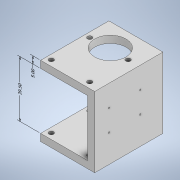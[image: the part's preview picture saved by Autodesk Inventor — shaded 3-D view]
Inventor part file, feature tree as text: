
AUTODESK INVENTOR PART (.ipt)
format: ipt  version: 2022 (Build 260153000, 153)  size: 168,448 bytes
history: native  units: mm
features: sketch x5, other x3, hole x3, extrude x2
ambient origin geometry x8: Origin, YZ Plane, XZ Plane, XY Plane, X Axis, Y Axis, Z Axis, Center Point
bodies: Body1 (feature_tree)
feature tree (13):
  other  "ソリッド1"
  extrude  "押し出し1"  Depth=48.0mm
  extrude  "押し出し2"  Depth=38.0mm
  hole  "穴1"  [1 undecoded]
  hole  "穴2"  [1 undecoded]
  hole  "穴4"  [1 undecoded]
  sketch  "スケッチ1"
  sketch  "スケッチ2"
  sketch  "スケッチ3"
  sketch  "スケッチ4"
  sketch  "スケッチ6"
  other  "長さ寸法 1"
  other  "長さ寸法 2"
note: 3 required parameter values undecoded (feature->parameter linkage not recoverable at this tier; creation-order binding heuristic only, values carry confidence <= 0.55)
